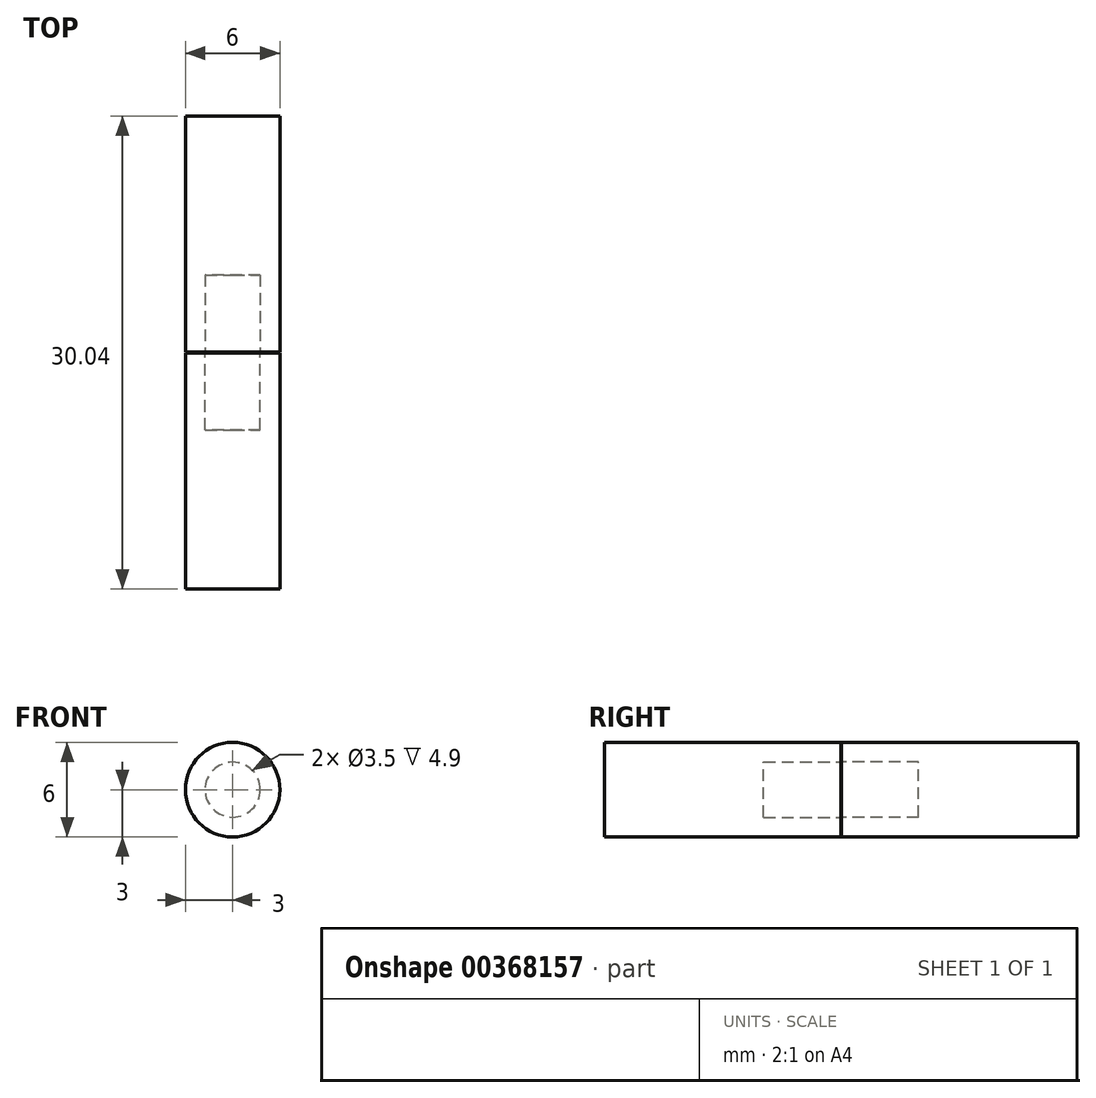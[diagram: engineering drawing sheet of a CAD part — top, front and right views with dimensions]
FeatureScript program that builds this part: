
annotation { "Feature Type Name" : "Feature", "Feature Type Description" : "" }
export const myFeature = defineFeature(function(context is Context, id is Id, definition is map)
    precondition{}
    {
        {
            var Q0;
            Q0=qCreatedBy(makeId("Front.planeOp"),FACE);
            var sketch = newSketch(context, id + "F0", { "sketchPlane" : qUnion([Q0])});
            skCircle(sketch, "E0", {"center": v(0, 0) * mm, "radius": 3 * mm});
            skCircle(sketch, "E1", {"center": v(0, 0) * mm, "radius": 1.75 * mm});
            skSolve(sketch);
        }
        {
            var Q0;
            Q0 = qSketchRegion(id + "F0", true);
            var Q1;
            Q1=makeQuery(id+"F0.imprint","IMPRINT",FACE,{"disambiguationData":[TD([[makeQuery(id+"F0.imprint","IMPRINT",EDGE,{"derivedFrom":sQuery(id+"F0.wireOp",EDGE,"E0")}),1.0]])]});
            var Q2;
            Q2=makeQuery(id+"F0.imprint","IMPRINT",FACE,{"disambiguationData":[TD([[makeQuery(id+"F0.imprint","IMPRINT",EDGE,{"derivedFrom":sQuery(id+"F0.wireOp",EDGE,"E1")}),1.0]])]});
            extrude(context, id + "F1", {"entities" : qUnion([Q0, Q1, Q2]), "depth" : 15 * mm});
        }
        {
            var Q0;
            Q0=makeQuery(id+"F0.imprint","IMPRINT",FACE,{"disambiguationData":[TD([[makeQuery(id+"F0.imprint","IMPRINT",EDGE,{"derivedFrom":sQuery(id+"F0.wireOp",EDGE,"E1")}),1.0]])]});
            extrude(context, id + "F2", {"entities" : qUnion([Q0]), "operationType" : NewBodyOperationType.REMOVE, "depth" : 4.9 * mm});
        }
        {
            var Q0;
            Q0=makeQuery(id+"F0.imprint","IMPRINT",FACE,{"disambiguationData":[TD([[makeQuery(id+"F0.imprint","IMPRINT",EDGE,{"derivedFrom":sQuery(id+"F0.wireOp",EDGE,"E0")}),1.0]])]});
            cPlane(context, id + "F3", {"entities" : qUnion([Q0]), "cplaneType" : CPlaneType.OFFSET, "offset" : 0.02 * mm, "oppositeDirection" : true, "width" : 150 * mm, "height" : 150 * mm});
        }
        {
            var Q0;
            Q0=makeQuery(id+"F1.opExtrude","SWEPT_BODY",BODY,{"disambiguationData":[OSD([sQuery(id+"F0.wireOp",EDGE,"E0")])]});
            var Q1;
            Q1=qCreatedBy(id+"F3.planeOp",FACE);
            mirror(context, id + "F4", {"entities" : qUnion([Q0]), "mirrorPlane" : qUnion([Q1])});
        }
    });
